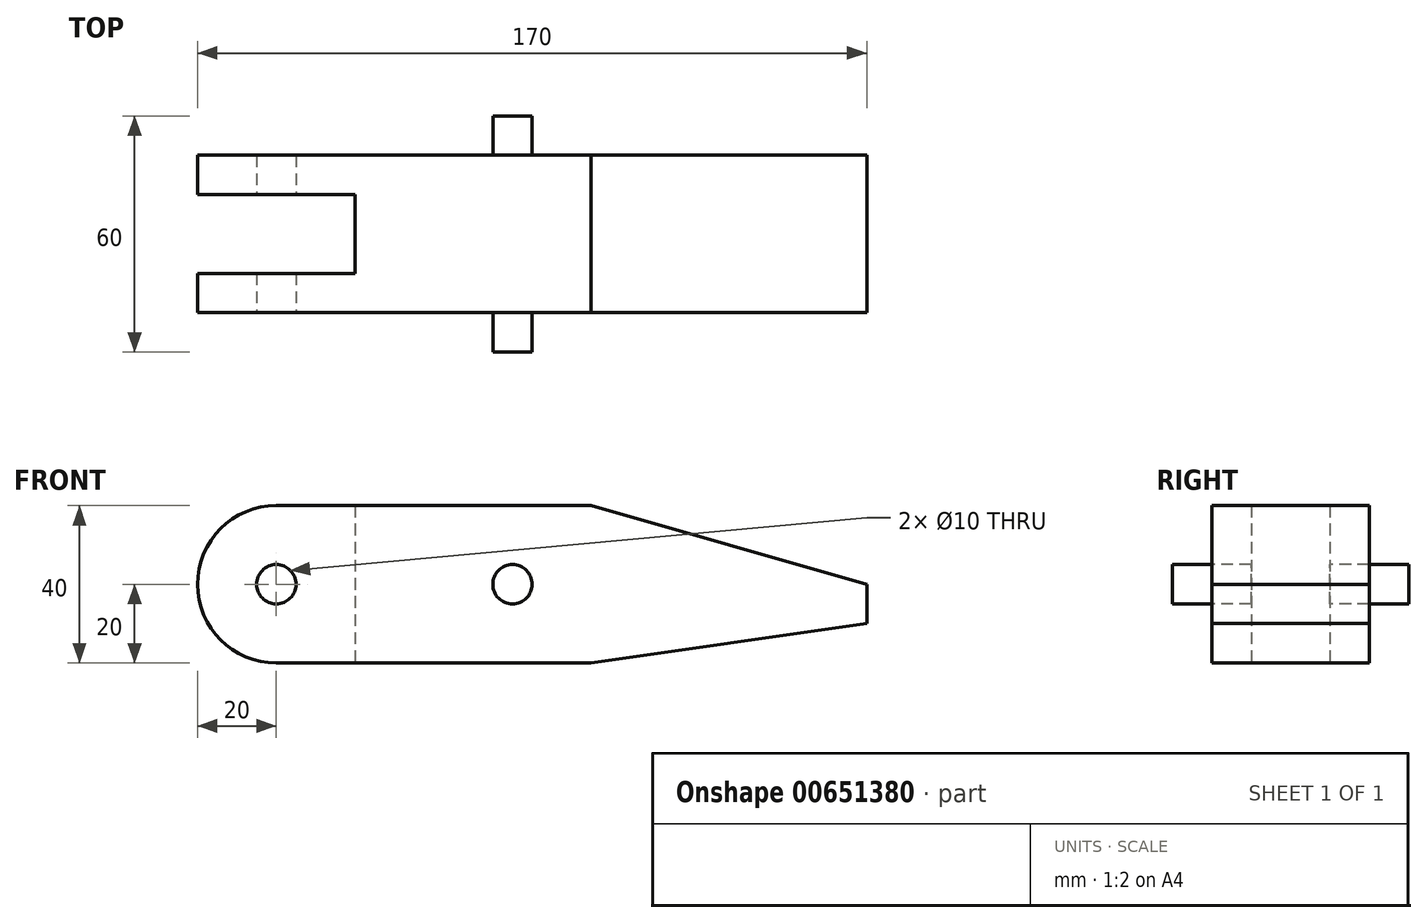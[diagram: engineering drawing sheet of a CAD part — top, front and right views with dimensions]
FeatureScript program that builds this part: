
annotation { "Feature Type Name" : "Feature", "Feature Type Description" : "" }
export const myFeature = defineFeature(function(context is Context, id is Id, definition is map)
    precondition{}
    {
        {
            var Q0;
            Q0=qCreatedBy(makeId("Right.planeOp"),FACE);
            var sketch = newSketch(context, id + "F0", { "sketchPlane" : qUnion([Q0])});
            skLineSegment(sketch, "E0.bottom", {"start": v(20, 20) * mm, "end": v(-20, 20) * mm});
            skLineSegment(sketch, "E0.top", {"start": v(20, -20) * mm, "end": v(-20, -20) * mm});
            skLineSegment(sketch, "E0.left", {"start": v(20, 20) * mm, "end": v(20, -20) * mm});
            skLineSegment(sketch, "E0.right", {"start": v(-20, 20) * mm, "end": v(-20, -20) * mm});
            skPoint(sketch, "E0.middle", {"position": v(0, 0) * mm});
            skSolve(sketch);
        }
        {
            var Q0;
            Q0 = qSketchRegion(id + "F0", true);
            extrude(context, id + "F1", {"entities" : qUnion([Q0]), "depth" : 80 * mm, "offsetDistance" : 25 * mm});
        }
        {
            var Q0;
            Q0=makeQuery(id+"F1.opExtrude","CAP_FACE",FACE,{"disambiguationData":[OSD([sQuery(id+"F0.wireOp",EDGE,"E0.bottom"),sQuery(id+"F0.wireOp",EDGE,"E0.top"),sQuery(id+"F0.wireOp",EDGE,"E0.left"),sQuery(id+"F0.wireOp",EDGE,"E0.right")])],"isStart":true});
            var sketch = newSketch(context, id + "F2", { "sketchPlane" : qUnion([Q0])});
            skLineSegment(sketch, "E1.bottom", {"start": v(10, 20) * mm, "end": v(-10, 20) * mm, "construction": true});
            skLineSegment(sketch, "E1.top", {"start": v(10, -20) * mm, "end": v(-10, -20) * mm, "construction": true});
            skLineSegment(sketch, "E1.left", {"start": v(10, 20) * mm, "end": v(10, -20) * mm});
            skLineSegment(sketch, "E1.right", {"start": v(-10, 20) * mm, "end": v(-10, -20) * mm});
            skPoint(sketch, "E1.middle", {"position": v(0, 0) * mm});
            skLineSegment(sketch, "E2.bottom", {"start": v(10, 20) * mm, "end": v(20, 20) * mm});
            skLineSegment(sketch, "E2.top", {"start": v(10, -20) * mm, "end": v(20, -20) * mm});
            skLineSegment(sketch, "E2.right", {"start": v(20, 20) * mm, "end": v(20, -20) * mm});
            skLineSegment(sketch, "E3.bottom", {"start": v(-10, -20) * mm, "end": v(-20, -20) * mm});
            skLineSegment(sketch, "E3.top", {"start": v(-10, 20) * mm, "end": v(-20, 20) * mm});
            skLineSegment(sketch, "E3.left", {"start": v(-10, -20) * mm, "end": v(-10, 20) * mm});
            skLineSegment(sketch, "E3.right", {"start": v(-20, -20) * mm, "end": v(-20, 20) * mm});
            skSolve(sketch);
        }
        {
            var Q0;
            Q0=makeQuery(id+"F2.imprint","IMPRINT",FACE,{"disambiguationData":[TD([[makeQuery(id+"F2.imprint","IMPRINT",EDGE,{"derivedFrom":sQuery(id+"F2.wireOp",EDGE,"E2.bottom")}),-1.0]])]});
            var Q1;
            Q1=makeQuery(id+"F2.imprint","IMPRINT",FACE,{"disambiguationData":[TD([[makeQuery(id+"F2.imprint","IMPRINT",EDGE,{"derivedFrom":sQuery(id+"F2.wireOp",EDGE,"E3.bottom")}),1.0]])]});
            extrude(context, id + "F3", {"entities" : qUnion([Q0, Q1]), "operationType" : NewBodyOperationType.ADD, "depth" : 40 * mm, "offsetDistance" : 25 * mm});
        }
        {
            var Q0;
            Q0=makeQuery(id+"F3.opExtrude","CAP_EDGE",EDGE,{"disambiguationData":[OSD([sQuery(id+"F2.wireOp",EDGE,"E3.top")])],"isStart":false});
            var Q1;
            Q1=makeQuery(id+"F3.opExtrude","CAP_EDGE",EDGE,{"disambiguationData":[OSD([sQuery(id+"F2.wireOp",EDGE,"E3.bottom")])],"isStart":false});
            var Q2;
            Q2=makeQuery(id+"F3.opExtrude","CAP_EDGE",EDGE,{"disambiguationData":[OSD([sQuery(id+"F2.wireOp",EDGE,"E2.bottom")])],"isStart":false});
            var Q3;
            Q3=makeQuery(id+"F3.opExtrude","CAP_EDGE",EDGE,{"disambiguationData":[OSD([sQuery(id+"F2.wireOp",EDGE,"E2.top")])],"isStart":false});
            fillet(context, id + "F4", {"entities" : qUnion([Q0, Q1, Q2, Q3]), "radius" : 20 * mm, "tangentPropagation" : true, "allowEdgeOverflow" : false});
        }
        {
            var Q0;
            Q0=makeQuery(id+"F3.boolean.opBoolean","MERGE",FACE,{"derivedFrom":[makeQuery(id+"F1.opExtrude","SWEPT_FACE",FACE,{"disambiguationData":[OSD([sQuery(id+"F0.wireOp",EDGE,"E0.right")])]}),makeQuery(id+"F3.opExtrude","SWEPT_FACE",FACE,{"disambiguationData":[OSD([sQuery(id+"F2.wireOp",EDGE,"E2.right")])]})]});
            var sketch = newSketch(context, id + "F5", { "sketchPlane" : qUnion([Q0])});
            skCircle(sketch, "E4", {"center": v(-20, 0) * mm, "radius": 5 * mm});
            skSolve(sketch);
        }
        {
            var Q0;
            Q0 = qSketchRegion(id + "F5", true);
            extrude(context, id + "F6", {"entities" : qUnion([Q0]), "operationType" : NewBodyOperationType.REMOVE, "endBound" : BoundingType.THROUGH_ALL, "oppositeDirection" : true, "depth" : 25 * mm, "offsetDistance" : 25 * mm});
        }
        {
            var Q0;
            Q0=qCreatedBy(makeId("Front.planeOp"),FACE);
            var sketch = newSketch(context, id + "F7", { "sketchPlane" : qUnion([Q0])});
            skCircle(sketch, "E5", {"center": v(40, 0) * mm, "radius": 5 * mm});
            skSolve(sketch);
        }
        {
            var Q0;
            Q0 = qSketchRegion(id + "F7", true);
            extrude(context, id + "F8", {"entities" : qUnion([Q0]), "operationType" : NewBodyOperationType.ADD, "endBound" : BoundingType.SYMMETRIC, "depth" : 60 * mm, "offsetDistance" : 25 * mm});
        }
        {
            var Q0;
            Q0=makeQuery(id+"F1.opExtrude","CAP_FACE",FACE,{"disambiguationData":[OSD([sQuery(id+"F0.wireOp",EDGE,"E0.bottom"),sQuery(id+"F0.wireOp",EDGE,"E0.top"),sQuery(id+"F0.wireOp",EDGE,"E0.left"),sQuery(id+"F0.wireOp",EDGE,"E0.right")])],"isStart":false});
            var sketch = newSketch(context, id + "F9", { "sketchPlane" : qUnion([Q0])});
            skLineSegment(sketch, "E6.0", {"start": v(20, 20) * mm, "end": v(-20, 20) * mm});
            skLineSegment(sketch, "E7.0", {"start": v(-20, 20) * mm, "end": v(-20, -20) * mm});
            skLineSegment(sketch, "E8.0", {"start": v(20, -20) * mm, "end": v(-20, -20) * mm});
            skLineSegment(sketch, "E9.0", {"start": v(20, 20) * mm, "end": v(20, -20) * mm});
            skSolve(sketch);
        }
        {
            var Q0;
            Q0=makeQuery(id+"F9.imprint","IMPRINT",FACE,{"disambiguationData":[TD([[makeQuery(id+"F9.imprint","IMPRINT",EDGE,{"derivedFrom":sQuery(id+"F9.wireOp",EDGE,"E6.0")}),1.0]])]});
            extrude(context, id + "F10", {"entities" : qUnion([Q0]), "operationType" : NewBodyOperationType.ADD, "depth" : 50 * mm, "offsetDistance" : 25 * mm});
        }
        {
            var Q0;
            Q0=makeQuery(id+"F10.boolean.opBoolean","MERGE",FACE,{"derivedFrom":[makeQuery(id+"F3.boolean.opBoolean","MERGE",FACE,{"derivedFrom":[makeQuery(id+"F1.opExtrude","SWEPT_FACE",FACE,{"disambiguationData":[OSD([sQuery(id+"F0.wireOp",EDGE,"E0.right")])]}),makeQuery(id+"F3.opExtrude","SWEPT_FACE",FACE,{"disambiguationData":[OSD([sQuery(id+"F2.wireOp",EDGE,"E2.right")])]})]}),makeQuery(id+"F10.opExtrude","SWEPT_FACE",FACE,{"disambiguationData":[OSD([sQuery(id+"F9.wireOp",EDGE,"E7.0")])]})]});
            var sketch = newSketch(context, id + "F11", { "sketchPlane" : qUnion([Q0])});
            skLineSegment(sketch, "E10", {"start": v(130, 0) * mm, "end": v(60, 20) * mm});
            skLineSegment(sketch, "E11", {"start": v(60, 20) * mm, "end": v(130, 20) * mm});
            skLineSegment(sketch, "E12", {"start": v(130, 20) * mm, "end": v(130, 0) * mm});
            skLineSegment(sketch, "E13", {"start": v(130, -10) * mm, "end": v(60, -20) * mm});
            skLineSegment(sketch, "E14", {"start": v(60, -20) * mm, "end": v(130, -20) * mm});
            skLineSegment(sketch, "E15", {"start": v(130, -20) * mm, "end": v(130, -10) * mm});
            skSolve(sketch);
        }
        {
            var Q0;
            Q0 = qSketchRegion(id + "F11", true);
            extrude(context, id + "F12", {"entities" : qUnion([Q0]), "operationType" : NewBodyOperationType.REMOVE, "endBound" : BoundingType.THROUGH_ALL, "oppositeDirection" : true, "depth" : 25 * mm, "offsetDistance" : 25 * mm});
        }
    });
